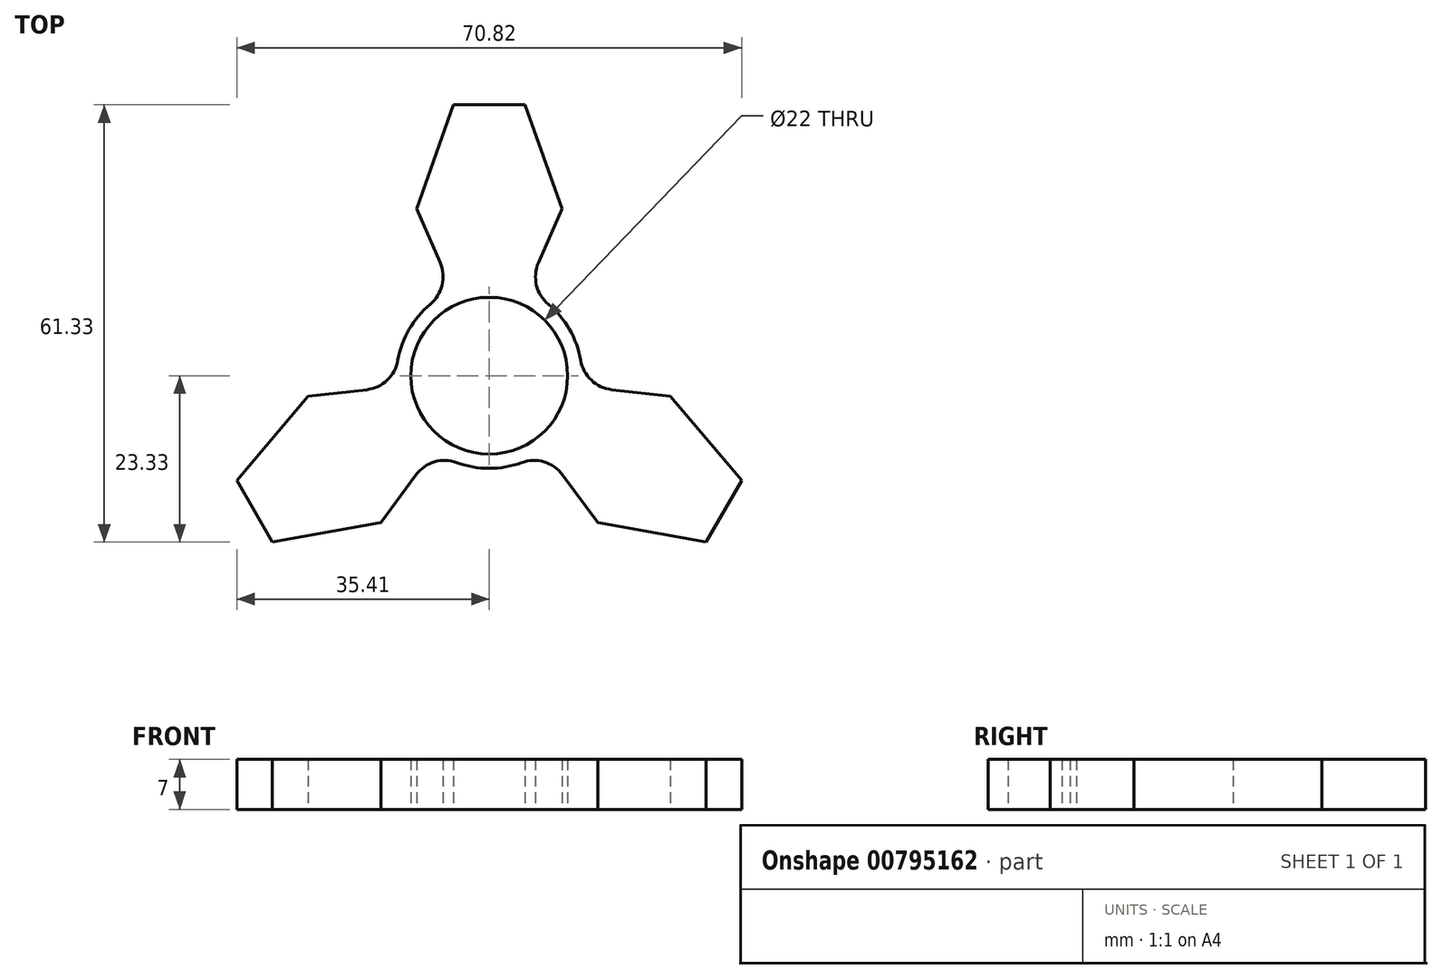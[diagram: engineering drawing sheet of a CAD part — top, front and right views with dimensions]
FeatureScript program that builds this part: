
annotation { "Feature Type Name" : "Feature", "Feature Type Description" : "" }
export const myFeature = defineFeature(function(context is Context, id is Id, definition is map)
    precondition{}
    {
        {
            var Q0;
            Q0=qCreatedBy(makeId("Top.planeOp"),FACE);
            var sketch = newSketch(context, id + "F0", { "sketchPlane" : qUnion([Q0])});
            skCircle(sketch, "E0", {"center": v(0, 0) * mm, "radius": 11 * mm});
            skArc(sketch, "E1", {"start": v(-8.3, 10.01) * mm, "mid": v(-11.26, 6.5) * mm, "end": v(-12.82, 2.18) * mm});
            skLineSegment(sketch, "E2", {"start": v(-5, 38) * mm, "end": v(5, 38) * mm});
            skLineSegment(sketch, "E3", {"start": v(-5, 38) * mm, "end": v(-10.2, 23.45) * mm});
            skLineSegment(sketch, "E4", {"start": v(5, 38) * mm, "end": v(10.2, 23.45) * mm});
            skLineSegment(sketch, "E5", {"start": v(-10.2, 23.45) * mm, "end": v(-6.9, 15.86) * mm});
            skLineSegment(sketch, "E6", {"start": v(10.2, 23.45) * mm, "end": v(6.9, 15.86) * mm});
            skPoint(sketch, "E7.orphan", {"position": v(-15.4, 8.9) * mm});
            skPoint(sketch, "E8.orphan", {"position": v(15.4, 8.9) * mm});
            skLineSegment(sketch, "E9.1.0", {"start": v(-35.4, -14.67) * mm, "end": v(-25.4, -2.89) * mm});
            skLineSegment(sketch, "E9.1.2", {"start": v(-25.4, -2.89) * mm, "end": v(-17.18, -1.95) * mm});
            skLineSegment(sketch, "E9.1.4", {"start": v(-30.4, -23.33) * mm, "end": v(-15.2, -20.56) * mm});
            skLineSegment(sketch, "E9.1.5", {"start": v(-15.2, -20.56) * mm, "end": v(-10.28, -13.9) * mm});
            skLineSegment(sketch, "E9.1.6", {"start": v(-30.4, -23.33) * mm, "end": v(-35.4, -14.67) * mm});
            skPoint(sketch, "E9.1.7", {"position": v(0, -17.79) * mm});
            skLineSegment(sketch, "E9.2.0", {"start": v(30.4, -23.33) * mm, "end": v(15.2, -20.56) * mm});
            skPoint(sketch, "E9.2.1", {"position": v(0, -17.79) * mm});
            skLineSegment(sketch, "E9.2.2", {"start": v(15.2, -20.56) * mm, "end": v(10.28, -13.9) * mm});
            skLineSegment(sketch, "E9.2.4", {"start": v(35.4, -14.67) * mm, "end": v(25.4, -2.89) * mm});
            skLineSegment(sketch, "E9.2.5", {"start": v(25.4, -2.89) * mm, "end": v(17.18, -1.95) * mm});
            skLineSegment(sketch, "E9.2.6", {"start": v(35.4, -14.67) * mm, "end": v(30.4, -23.33) * mm});
            skPoint(sketch, "E10.start.orphan", {"position": v(0, 38) * mm});
            skArc(sketch, "E11.trimOffspring", {"start": v(-4.52, -12.19) * mm, "mid": v(0, -13) * mm, "end": v(4.52, -12.19) * mm});
            skArc(sketch, "E12.trimOffspring", {"start": v(12.82, 2.18) * mm, "mid": v(11.26, 6.5) * mm, "end": v(8.3, 10.01) * mm});
            skPoint(sketch, "E13.visualSharp", {"position": v(-5.19, 11.92) * mm});
            skArc(sketch, "E13.filletArc", {"start": v(-8.3, 10.01) * mm, "mid": v(-6.62, 12.7) * mm, "end": v(-6.9, 15.86) * mm});
            skPoint(sketch, "E14.visualSharp", {"position": v(-12.92, -1.47) * mm});
            skArc(sketch, "E14.filletArc", {"start": v(-17.18, -1.95) * mm, "mid": v(-14.3, -0.62) * mm, "end": v(-12.82, 2.18) * mm});
            skPoint(sketch, "E15.visualSharp", {"position": v(-7.73, -10.45) * mm});
            skArc(sketch, "E15.filletArc", {"start": v(-4.52, -12.19) * mm, "mid": v(-7.69, -12.08) * mm, "end": v(-10.28, -13.9) * mm});
            skPoint(sketch, "E16.visualSharp", {"position": v(7.73, -10.45) * mm});
            skArc(sketch, "E16.filletArc", {"start": v(10.28, -13.9) * mm, "mid": v(7.69, -12.08) * mm, "end": v(4.52, -12.19) * mm});
            skPoint(sketch, "E17.visualSharp", {"position": v(12.92, -1.47) * mm});
            skArc(sketch, "E17.filletArc", {"start": v(12.82, 2.18) * mm, "mid": v(14.3, -0.62) * mm, "end": v(17.18, -1.95) * mm});
            skPoint(sketch, "E18.visualSharp", {"position": v(5.19, 11.92) * mm});
            skArc(sketch, "E18.filletArc", {"start": v(6.9, 15.86) * mm, "mid": v(6.62, 12.7) * mm, "end": v(8.3, 10.01) * mm});
            skSolve(sketch);
        }
        {
            var Q0;
            Q0=makeQuery(id+"F0.imprint","IMPRINT",FACE,{"disambiguationData":[TD([[makeQuery(id+"F0.imprint","IMPRINT",EDGE,{"derivedFrom":sQuery(id+"F0.wireOp",EDGE,"E0")}),-1.0]])]});
            extrude(context, id + "F1", {"entities" : qUnion([Q0]), "depth" : 7 * mm, "offsetDistance" : 25 * mm});
        }
    });
